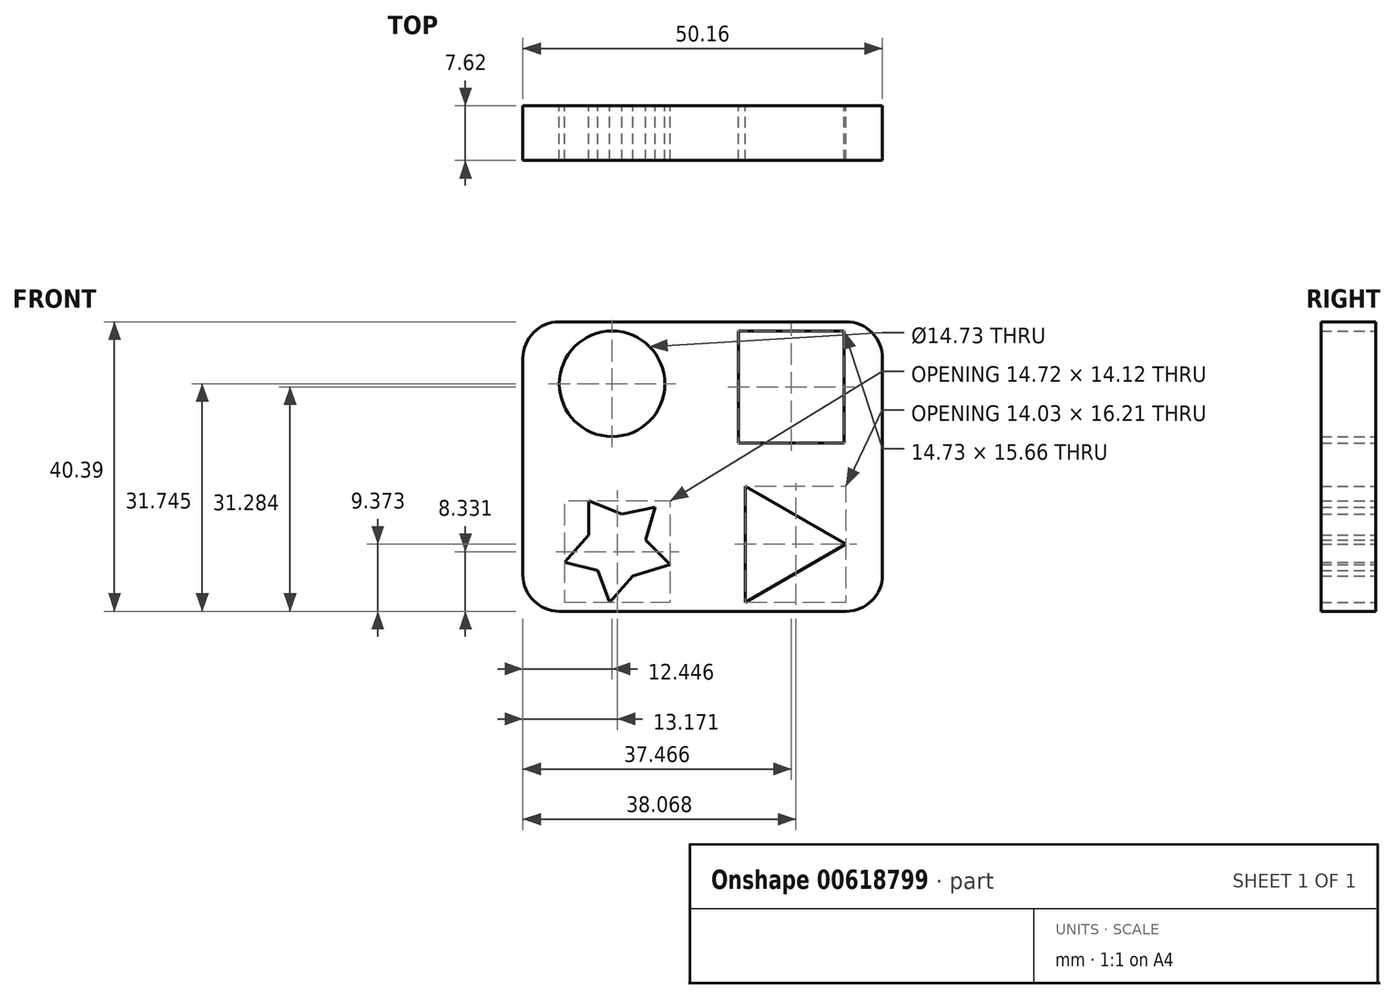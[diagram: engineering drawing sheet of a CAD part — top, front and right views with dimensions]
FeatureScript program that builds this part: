
annotation { "Feature Type Name" : "Feature", "Feature Type Description" : "" }
export const myFeature = defineFeature(function(context is Context, id is Id, definition is map)
    precondition{}
    {
        {
            var Q0;
            Q0=qCreatedBy(makeId("Front.planeOp"),FACE);
            var sketch = newSketch(context, id + "F0", { "sketchPlane" : qUnion([Q0])});
            skLineSegment(sketch, "E0.bottom", {"start": v(5.08, 0) * mm, "end": v(45.08, 0) * mm});
            skLineSegment(sketch, "E0.top", {"start": v(5.08, 40.39) * mm, "end": v(45.09, 40.39) * mm});
            skLineSegment(sketch, "E0.left", {"start": v(0, 5.08) * mm, "end": v(0, 35.3) * mm});
            skLineSegment(sketch, "E0.right", {"start": v(50.17, 5.08) * mm, "end": v(50.17, 35.3) * mm});
            skPoint(sketch, "E1.visualSharp", {"position": v(0, 40.39) * mm});
            skArc(sketch, "E1.filletArc", {"start": v(5.08, 40.39) * mm, "mid": v(1.49, 38.9) * mm, "end": v(0, 35.3) * mm});
            skPoint(sketch, "E2.visualSharp", {"position": v(50.16, 40.39) * mm});
            skArc(sketch, "E2.filletArc", {"start": v(50.16, 35.3) * mm, "mid": v(48.68, 38.9) * mm, "end": v(45.09, 40.39) * mm});
            skPoint(sketch, "E3.visualSharp", {"position": v(50.16, 0) * mm});
            skArc(sketch, "E3.filletArc", {"start": v(45.09, 0) * mm, "mid": v(48.68, 1.49) * mm, "end": v(50.17, 5.08) * mm});
            skPoint(sketch, "E4.visualSharp", {"position": v(0, 0) * mm});
            skArc(sketch, "E4.filletArc", {"start": v(0, 5.08) * mm, "mid": v(1.49, 1.49) * mm, "end": v(5.08, 0) * mm});
            skLineSegment(sketch, "E5.left", {"start": v(44.83, 39.12) * mm, "end": v(44.83, 23.54) * mm});
            skLineSegment(sketch, "E6.bottom", {"start": v(44.83, 39.12) * mm, "end": v(30.1, 39.12) * mm});
            skLineSegment(sketch, "E6.top", {"start": v(44.83, 23.45) * mm, "end": v(30.1, 23.45) * mm});
            skLineSegment(sketch, "E6.left", {"start": v(44.83, 39.12) * mm, "end": v(44.83, 23.45) * mm});
            skLineSegment(sketch, "E6.right", {"start": v(30.1, 39.12) * mm, "end": v(30.1, 23.45) * mm});
            skLineSegment(sketch, "E7", {"start": v(31.05, 1.27) * mm, "end": v(31.05, 17.48) * mm});
            skLineSegment(sketch, "E8", {"start": v(31.05, 1.27) * mm, "end": v(45.09, 9.37) * mm});
            skLineSegment(sketch, "E9", {"start": v(45.09, 9.37) * mm, "end": v(31.05, 17.48) * mm});
            skCircle(sketch, "E10", {"center": v(12.45, 31.74) * mm, "radius": 7.37 * mm});
            skLineSegment(sketch, "E11", {"start": v(0, 0) * mm, "end": v(12.4, 0) * mm});
            skLineSegment(sketch, "E12", {"start": v(12.1, 1.27) * mm, "end": v(15.32, 4.92) * mm});
            skLineSegment(sketch, "E13", {"start": v(15.32, 4.92) * mm, "end": v(20.53, 6.52) * mm});
            skLineSegment(sketch, "E14", {"start": v(12.1, 1.27) * mm, "end": v(10.43, 5.72) * mm});
            skPoint(sketch, "E14.endSnap0", {"position": v(17.92, 5.72) * mm});
            skLineSegment(sketch, "E15", {"start": v(10.43, 5.72) * mm, "end": v(5.81, 6.82) * mm});
            skLineSegment(sketch, "E16", {"start": v(20.53, 6.52) * mm, "end": v(17.13, 9.93) * mm});
            skLineSegment(sketch, "E17", {"start": v(17.13, 9.93) * mm, "end": v(18.44, 14.5) * mm});
            skLineSegment(sketch, "E18", {"start": v(9.15, 15.4) * mm, "end": v(9.15, 10.65) * mm});
            skLineSegment(sketch, "E19", {"start": v(9.15, 10.65) * mm, "end": v(5.81, 6.82) * mm});
            skLineSegment(sketch, "E20", {"start": v(9.15, 15.4) * mm, "end": v(13.8, 13.58) * mm});
            skPoint(sketch, "E20.endSnap0", {"position": v(13.8, 14.95) * mm});
            skLineSegment(sketch, "E21", {"start": v(13.8, 13.58) * mm, "end": v(18.44, 14.5) * mm});
            skSolve(sketch);
        }
        {
            var Q0;
            {var subQ1=sQuery(id+"F0.wireOp",EDGE,"E0.bottom");Q0=makeQuery(id+"F0.imprint","IMPRINT",FACE,{"disambiguationData":[TD([[makeQuery(id+"F0.imprint","IMPRINT",EDGE,{"derivedFrom":subQ1}),1.0]])]});}
            extrude(context, id + "F1", {"entities" : qUnion([Q0]), "depth" : 7.62 * mm, "offsetDistance" : 25.4 * mm});
        }
    });
